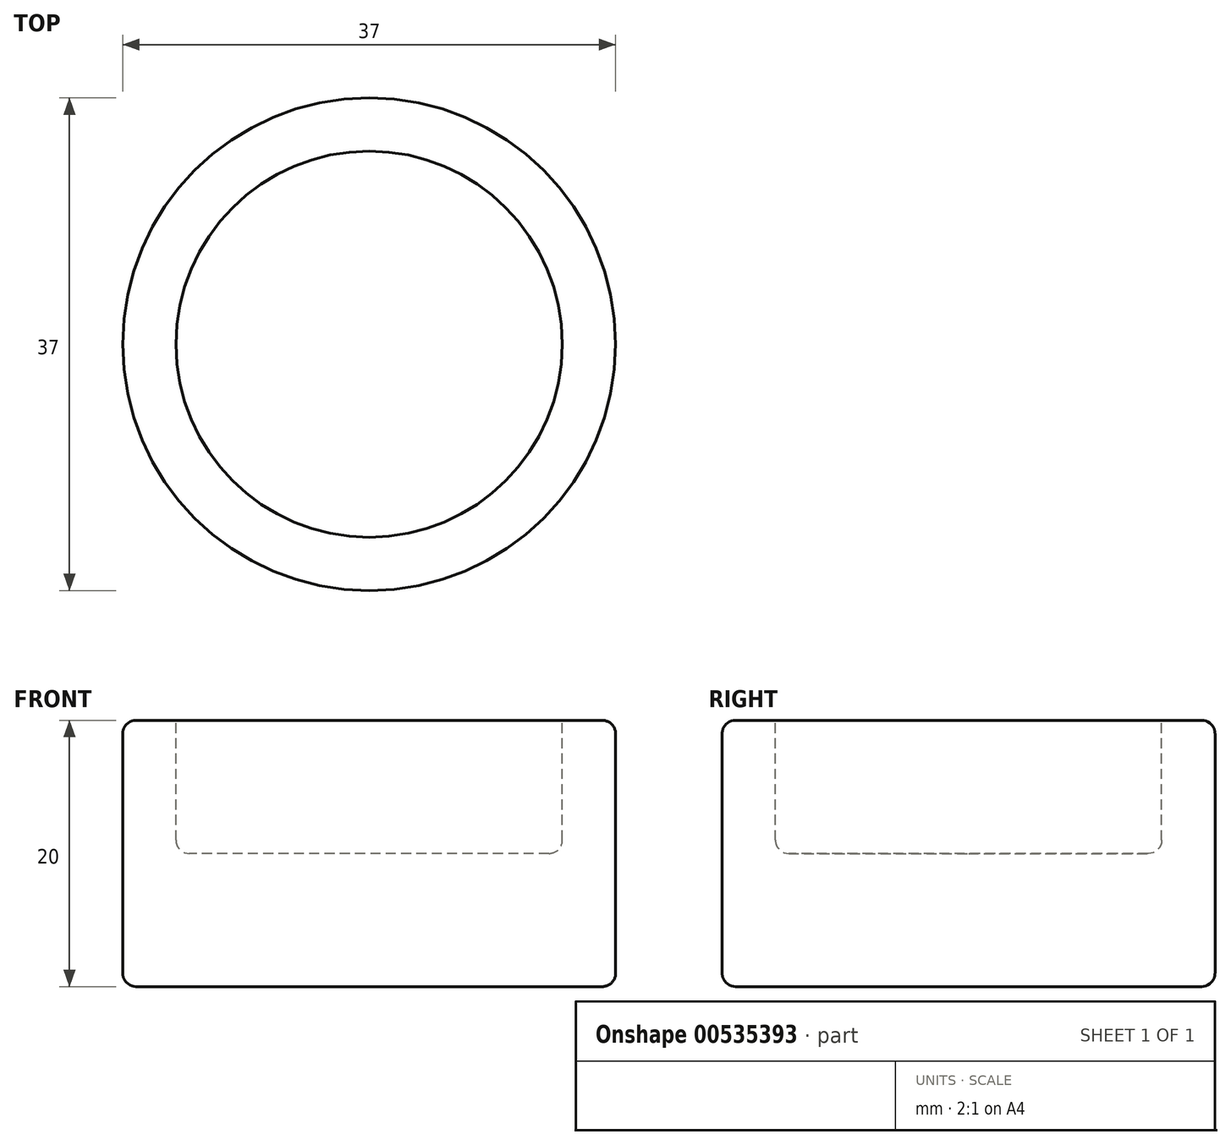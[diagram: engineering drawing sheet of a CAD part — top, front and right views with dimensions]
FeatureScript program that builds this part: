
annotation { "Feature Type Name" : "Feature", "Feature Type Description" : "" }
export const myFeature = defineFeature(function(context is Context, id is Id, definition is map)
    precondition{}
    {
        {
            var Q0;
            Q0=qCreatedBy(makeId("Top.planeOp"),FACE);
            var sketch = newSketch(context, id + "F0", { "sketchPlane" : qUnion([Q0])});
            skCircle(sketch, "E0", {"center": v(0, 0) * mm, "radius": 18.5 * mm});
            skSolve(sketch);
        }
        {
            var Q0;
            Q0=qSketchRegion(id+"F0",true);
            extrude(context, id + "F1", {"entities" : qUnion([Q0]), "depth" : 20 * mm, "offsetDistance" : 25 * mm});
        }
        {
            var Q0;
            Q0=makeQuery(id+"F1.opExtrude","CAP_FACE",FACE,{"disambiguationData":[OSD([sQuery(id+"F0.wireOp",EDGE,"E0")])],"isStart":false});
            var sketch = newSketch(context, id + "F2", { "sketchPlane" : qUnion([Q0])});
            skCircle(sketch, "E1", {"center": v(0, 0) * mm, "radius": 14.5 * mm});
            skSolve(sketch);
        }
        {
            var Q0;
            Q0=qSketchRegion(id+"F2",true);
            extrude(context, id + "F3", {"entities" : qUnion([Q0]), "operationType" : NewBodyOperationType.REMOVE, "oppositeDirection" : true, "depth" : 10 * mm, "offsetDistance" : 25 * mm});
        }
        {
            var Q0;
            Q0=makeQuery(id+"F1.opExtrude","CAP_EDGE",EDGE,{"disambiguationData":[OSD([sQuery(id+"F0.wireOp",EDGE,"E0")])],"isStart":false});
            var Q1;
            Q1=makeQuery(id+"F3.boolean.opBoolean","COPY",EDGE,{"derivedFrom":makeQuery(id+"F3.opExtrude","CAP_EDGE",EDGE,{"disambiguationData":[OSD([sQuery(id+"F2.wireOp",EDGE,"E1")])],"isStart":true})});
            var Q2;
            Q2=makeQuery(id+"F1.opExtrude","CAP_EDGE",EDGE,{"disambiguationData":[OSD([sQuery(id+"F0.wireOp",EDGE,"E0")])],"isStart":true});
            var Q3;
            Q3=makeQuery(id+"F3.boolean.opBoolean","COPY",EDGE,{"derivedFrom":makeQuery(id+"F3.opExtrude","CAP_EDGE",EDGE,{"disambiguationData":[OSD([sQuery(id+"F2.wireOp",EDGE,"E1")])],"isStart":false})});
            fillet(context, id + "F4", {"entities" : qUnion([Q0, Q1, Q2, Q3]), "radius" : 1 * mm, "tangentPropagation" : true, "allowEdgeOverflow" : false});
        }
    });
